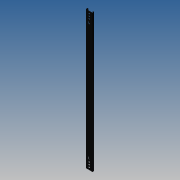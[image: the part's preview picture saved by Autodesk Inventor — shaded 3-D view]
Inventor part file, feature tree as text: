
AUTODESK INVENTOR PART (.ipt)
format: ipt  version: 2011 (Build 150239000, 239)  size: 397,312 bytes
history: native  units: mm
features: fillet x10, extrude x6, sketch x6, chamfer x1
ambient origin geometry x8: Origin, YZ Plane, XZ Plane, XY Plane, X Axis, Y Axis, Z Axis, Center Point
bodies: Solid1 (feature_tree)
feature tree (23):
  extrude  "Extrusion1"  Depth=2.0mm
  extrude  "Extrusion2"  Depth=2.0mm
  chamfer  "Chamfer1"  Distance=1.0mm
  extrude  "Extrusion3"  TaperAngle=90.0deg  [1 undecoded]
  extrude  "Extrusion4"  TaperAngle=45.0deg  [1 undecoded]
  fillet  "Fillet1"  Radius=1.0mm
  fillet  "Fillet2"  Radius=2.5mm
  extrude  "Extrusion5"  TaperAngle=135.0deg  [1 undecoded]
  fillet  "Fillet3"  Radius=2.2mm
  fillet  "Fillet4"  Radius=0.2mm
  fillet  "Fillet5"  Radius=600.0mm
  extrude  "Extrusion6"  Depth=5.0mm
  fillet  "Fillet6"  Radius=5.0mm
  fillet  "Fillet7"  Radius=5.0mm
  fillet  "Fillet8"  Radius=10.0mm
  fillet  "Fillet9"  Radius=10.0mm
  fillet  "Fillet10"  Radius=5.0mm
  sketch  "Sketch1"  dims[d3=5.0mm d4=2.0mm]
  sketch  "Sketch2"  dims[d5=1.7mm d6=2.0mm]
  sketch  "Sketch4"  dims[d7=0.3mm]
  sketch  "Sketch5"  dims[d8=1.4mm]
  sketch  "Sketch6"  dims[d9=4.4mm]
  sketch  "Sketch7"  dims[d12=45.0deg d13=1.0mm d14=90.0deg d15=45.0deg d16=1.0mm d17=2.5mm d19=135.0deg d20=2.2mm d21=0.2mm d22=600.0mm d23=0.0mm d27=5.0mm d28=5.0mm d29=5.0mm d30=10.0mm d31=10.0mm d32=5.0mm d34=20.0mm d35=0.0mm d36=0.2mm d37=2.0mm d38=45.0deg d47=5.0mm d48=10.0mm d49=50.0mm d50=11.200015mm d51=11.200015mm d52=1.2mm d53=300.0mm d54=20.0mm d55=0.0mm d56=0.3mm d57=300.0mm d58=2.0mm d59=0.0mm d60=0.7mm d61=0.7mm d62=10.0mm d63=1.2mm d64=0.3mm d65=0.0mm d66=0.1mm d67=0.1mm d68=0.2mm d69=10.0mm d70=1.2mm d71=0.3mm d72=0.0mm d73=0.1mm d74=0.1mm d75=0.1mm d76=0.1mm d77=0.2mm]
note: 3 required parameter values undecoded (feature->parameter linkage not recoverable at this tier; creation-order binding heuristic only, values carry confidence <= 0.55)
